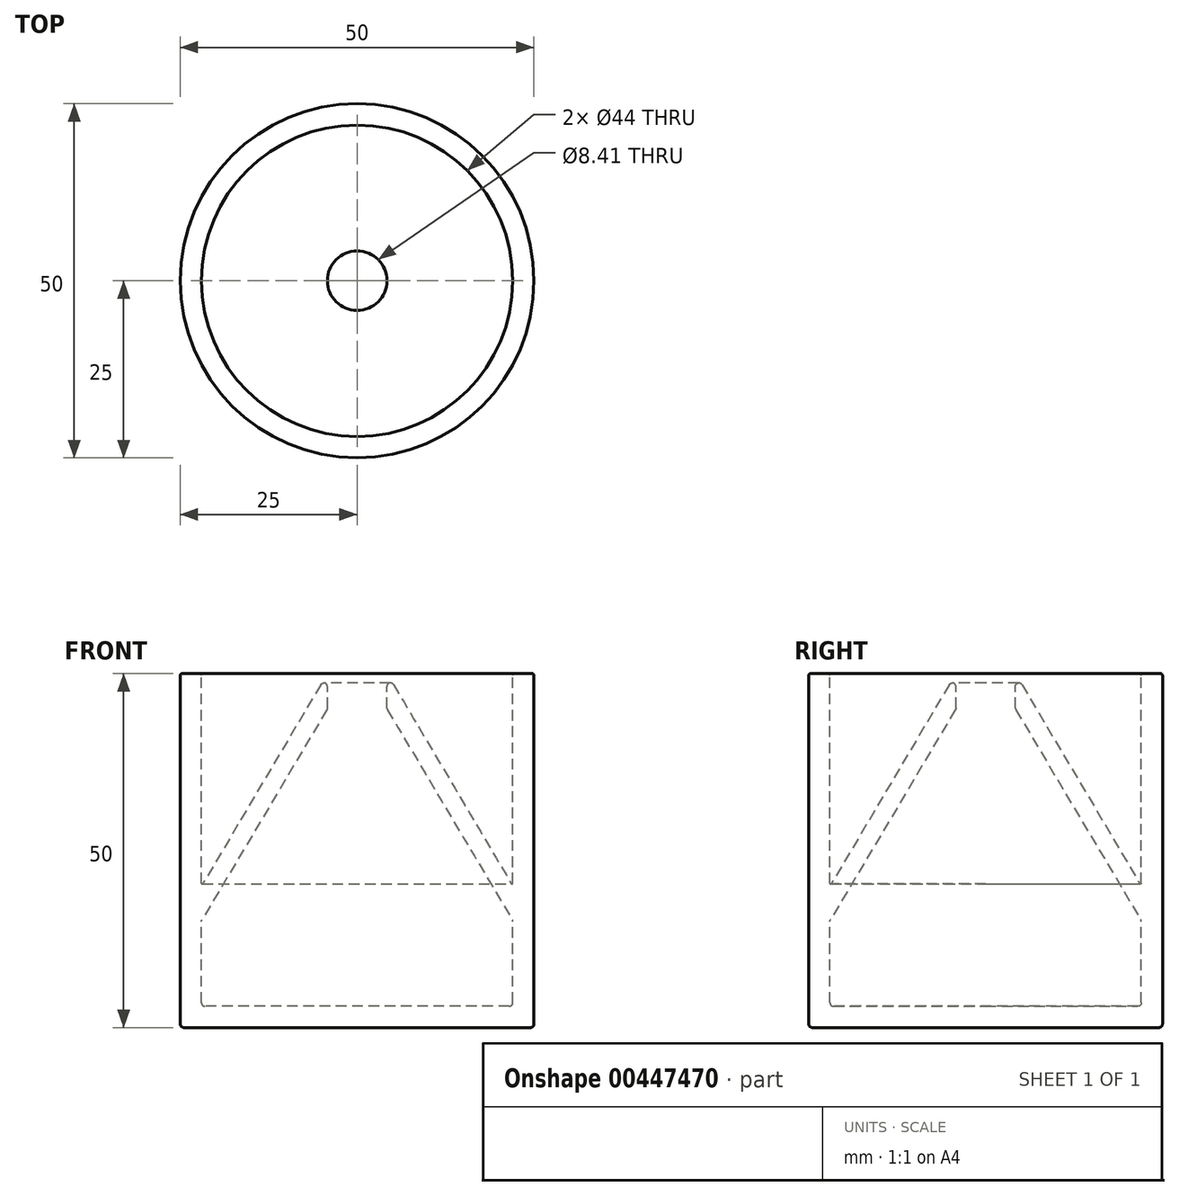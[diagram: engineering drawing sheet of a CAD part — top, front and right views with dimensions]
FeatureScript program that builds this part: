
annotation { "Feature Type Name" : "Feature", "Feature Type Description" : "" }
export const myFeature = defineFeature(function(context is Context, id is Id, definition is map)
    precondition{}
    {
        {
            var Q0;
            Q0=qCreatedBy(makeId("Front.planeOp"),FACE);
            var sketch = newSketch(context, id + "F0", { "sketchPlane" : qUnion([Q0])});
            skLineSegment(sketch, "E0", {"start": v(-25, 0.5) * mm, "end": v(-25, 49.75) * mm});
            skLineSegment(sketch, "E1", {"start": v(-24.75, 50) * mm, "end": v(-22.25, 50) * mm});
            skLineSegment(sketch, "E2", {"start": v(-22, 50) * mm, "end": v(-22, 50) * mm});
            skLineSegment(sketch, "E3", {"start": v(-21.5, 3) * mm, "end": v(0, 3) * mm});
            skLineSegment(sketch, "E4", {"start": v(0, 3) * mm, "end": v(0, 0) * mm});
            skLineSegment(sketch, "E5", {"start": v(0, 0) * mm, "end": v(-24.5, 0) * mm});
            skLineSegment(sketch, "E6", {"start": v(-22, 3.5) * mm, "end": v(-22, 14.97) * mm});
            skLineSegment(sketch, "E7", {"start": v(-21.93, 15.23) * mm, "end": v(-4.28, 44.88) * mm});
            skLineSegment(sketch, "E8", {"start": v(-4.2, 45.14) * mm, "end": v(-4.2, 48.18) * mm});
            skLineSegment(sketch, "E9", {"start": v(-5.14, 48.43) * mm, "end": v(-21.81, 20.31) * mm});
            skLineSegment(sketch, "E10", {"start": v(-22, 20.36) * mm, "end": v(-22, 49.75) * mm});
            skPoint(sketch, "E11.visualSharp", {"position": v(-4.2, 50) * mm});
            skArc(sketch, "E11.filletArc", {"start": v(-4.2, 48.18) * mm, "mid": v(-4.57, 48.66) * mm, "end": v(-5.14, 48.43) * mm});
            skPoint(sketch, "E12.visualSharp", {"position": v(-4.2, 45) * mm});
            skArc(sketch, "E12.filletArc", {"start": v(-4.28, 44.88) * mm, "mid": v(-4.22, 45) * mm, "end": v(-4.2, 45.14) * mm});
            skPoint(sketch, "E13.visualSharp", {"position": v(-22, 20) * mm});
            skArc(sketch, "E13.filletArc", {"start": v(-22, 20.36) * mm, "mid": v(-21.93, 20.27) * mm, "end": v(-21.81, 20.31) * mm});
            skPoint(sketch, "E14.visualSharp", {"position": v(-22, 15.11) * mm});
            skArc(sketch, "E14.filletArc", {"start": v(-21.93, 15.23) * mm, "mid": v(-21.98, 15.1) * mm, "end": v(-22, 14.97) * mm});
            skPoint(sketch, "E15.visualSharp", {"position": v(-22, 3) * mm});
            skArc(sketch, "E15.filletArc", {"start": v(-22, 3.5) * mm, "mid": v(-21.85, 3.15) * mm, "end": v(-21.5, 3) * mm});
            skPoint(sketch, "E16.visualSharp", {"position": v(-25, 0) * mm});
            skArc(sketch, "E16.filletArc", {"start": v(-25, 0.5) * mm, "mid": v(-24.85, 0.15) * mm, "end": v(-24.5, 0) * mm});
            skPoint(sketch, "E17.visualSharp", {"position": v(-25, 50) * mm});
            skArc(sketch, "E17.filletArc", {"start": v(-24.75, 50) * mm, "mid": v(-24.93, 49.93) * mm, "end": v(-25, 49.75) * mm});
            skPoint(sketch, "E18.visualSharp", {"position": v(-22, 50) * mm});
            skArc(sketch, "E18.filletArc", {"start": v(-22, 49.75) * mm, "mid": v(-22.07, 49.93) * mm, "end": v(-22.25, 50) * mm});
            skSolve(sketch);
        }
        {
            var Q0;
            Q0=makeQuery(id+"F0.imprint","IMPRINT",FACE,{"disambiguationData":[TD([[makeQuery(id+"F0.imprint","IMPRINT",EDGE,{"derivedFrom":sQuery(id+"F0.wireOp",EDGE,"E0")}),-1.0]])]});
            var Q1;
            Q1=sQuery(id+"F0.wireOp",EDGE,"E4");
            revolve(context, id + "F1", {"entities" : qUnion([Q0]), "axis" : qUnion([Q1]), "revolveType" : RevolveType.FULL});
        }
    });
